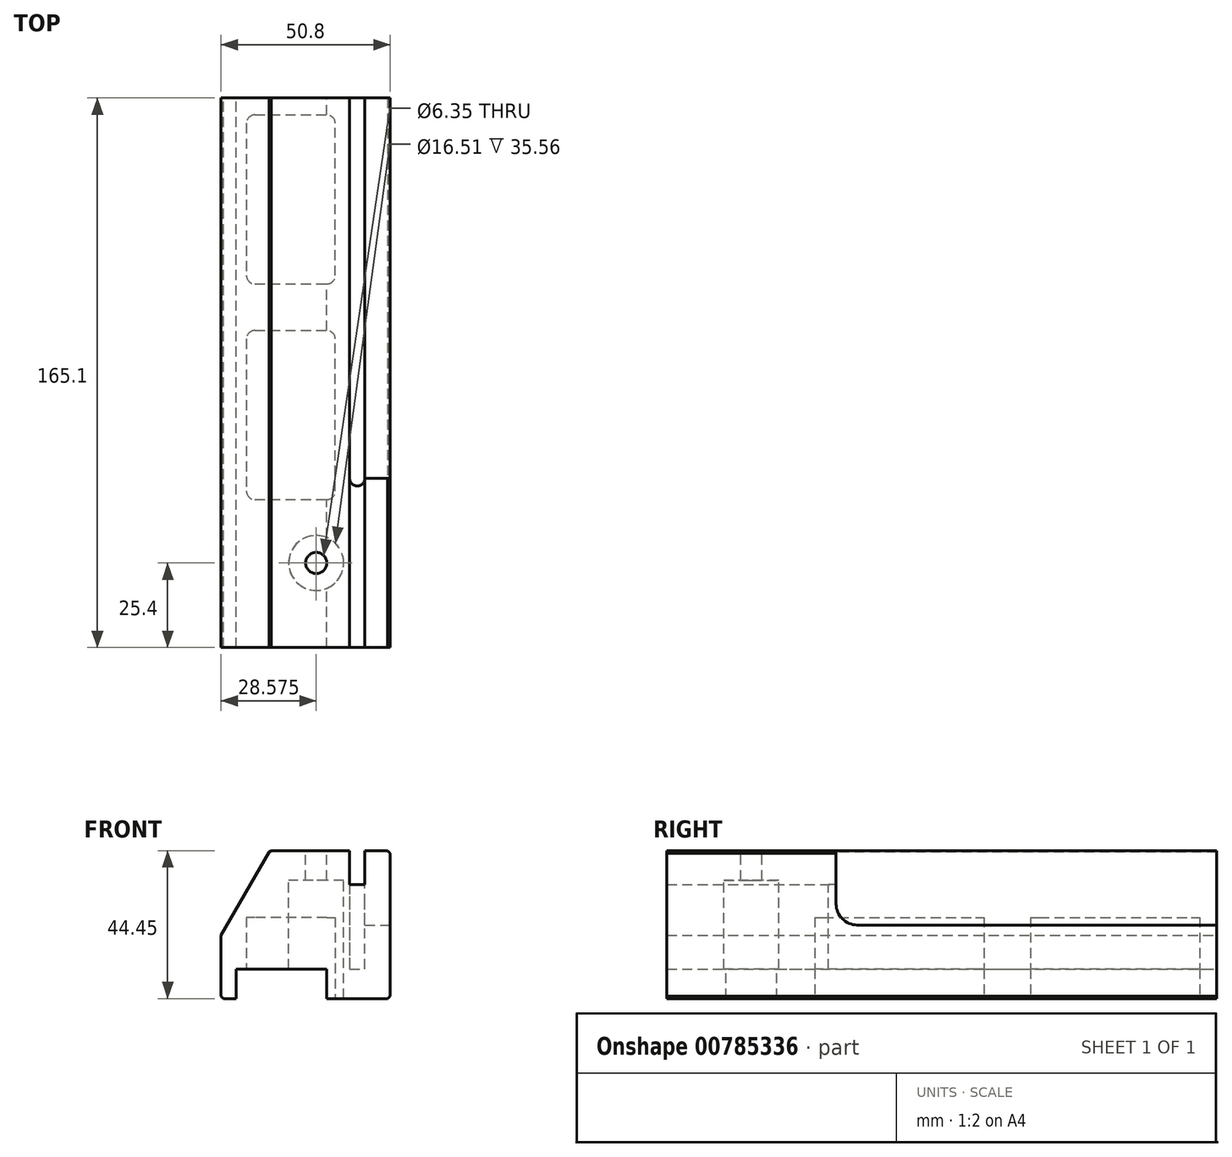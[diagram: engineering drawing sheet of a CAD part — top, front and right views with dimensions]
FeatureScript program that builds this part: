
annotation { "Feature Type Name" : "Feature", "Feature Type Description" : "" }
export const myFeature = defineFeature(function(context is Context, id is Id, definition is map)
    precondition{}
    {
        {
            var Q0;
            Q0=qCreatedBy(makeId("Front.planeOp"),FACE);
            var sketch = newSketch(context, id + "F0", { "sketchPlane" : qUnion([Q0])});
            skLineSegment(sketch, "E0.bottom", {"start": v(0, 0) * mm, "end": v(50.8, 0) * mm});
            skLineSegment(sketch, "E0.top", {"start": v(0, 44.45) * mm, "end": v(50.8, 44.45) * mm});
            skLineSegment(sketch, "E0.left", {"start": v(0, 0) * mm, "end": v(0, 44.45) * mm});
            skLineSegment(sketch, "E0.right", {"start": v(50.8, 0) * mm, "end": v(50.8, 44.45) * mm});
            skSolve(sketch);
        }
        {
            var Q0;
            Q0=qCreatedBy(makeId("Front.planeOp"),FACE);
            var sketch = newSketch(context, id + "F1", { "sketchPlane" : qUnion([Q0])});
            skLineSegment(sketch, "E1.bottom", {"start": v(4.57, 0) * mm, "end": v(31.75, 0) * mm});
            skLineSegment(sketch, "E1.top", {"start": v(4.57, 8.9) * mm, "end": v(31.75, 8.9) * mm});
            skLineSegment(sketch, "E1.left", {"start": v(4.57, 0) * mm, "end": v(4.57, 8.9) * mm});
            skLineSegment(sketch, "E1.right", {"start": v(31.75, 0) * mm, "end": v(31.75, 8.9) * mm});
            skSolve(sketch);
        }
        {
            var Q0;
            Q0=qCreatedBy(makeId("Front.planeOp"),FACE);
            var sketch = newSketch(context, id + "F2", { "sketchPlane" : qUnion([Q0])});
            skLineSegment(sketch, "E2.bottom", {"start": v(38.6, 44.45) * mm, "end": v(43.18, 44.45) * mm});
            skLineSegment(sketch, "E2.top", {"start": v(38.6, 34.3) * mm, "end": v(43.18, 34.3) * mm});
            skLineSegment(sketch, "E2.left", {"start": v(38.6, 44.45) * mm, "end": v(38.6, 34.3) * mm});
            skLineSegment(sketch, "E2.right", {"start": v(43.18, 44.45) * mm, "end": v(43.18, 34.3) * mm});
            skSolve(sketch);
        }
        {
            var Q0;
            Q0=qSketchRegion(id+"F0",true);
            extrude(context, id + "F3", {"entities" : qUnion([Q0]), "depth" : 165.1 * mm, "offsetDistance" : 25.4 * mm});
        }
        {
            var Q0;
            Q0=makeQuery(id+"F3.opExtrude","SWEPT_EDGE",EDGE,{"disambiguationData":[OSD([sQuery(id+"F0.wireOp",EDGE,"E0.top"),sQuery(id+"F0.wireOp",EDGE,"E0.left")])]});
            chamfer(context, id + "F4", {"entities" : qUnion([Q0]), "chamferType" : ChamferType.OFFSET_ANGLE, "width" : 25.4 * mm, "oppositeDirection" : false, "angle" : 30 * degree, "tangentPropagation" : true});
        }
        {
            var Q0;
            Q0=qSketchRegion(id+"F1",true);
            extrude(context, id + "F5", {"entities" : qUnion([Q0]), "operationType" : NewBodyOperationType.REMOVE, "depth" : 228.6 * mm, "offsetDistance" : 25.4 * mm});
        }
        {
            var Q0;
            Q0=qSketchRegion(id+"F2",true);
            extrude(context, id + "F6", {"entities" : qUnion([Q0]), "operationType" : NewBodyOperationType.REMOVE, "depth" : 228.6 * mm, "offsetDistance" : 25.4 * mm});
        }
        {
            var Q0;
            {var subQ0=sQuery(id+"F0.wireOp",EDGE,"E0.right");var subQ3=sQuery(id+"F0.wireOp",EDGE,"E0.bottom");Q0=makeQuery(id+"F5.boolean.opBoolean","SPLIT",FACE,{"disambiguationData":[TD([makeQuery(id+"F3.opExtrude","SWEPT_FACE",FACE,{"disambiguationData":[OSD([subQ0])]})])],"derivedFrom":makeQuery(id+"F3.opExtrude","SWEPT_FACE",FACE,{"disambiguationData":[OSD([subQ3])]})});}
            var sketch = newSketch(context, id + "F7", { "sketchPlane" : qUnion([Q0])});
            skLineSegment(sketch, "E3.bottom", {"start": v(31.75, 55.88) * mm, "end": v(10.16, 55.88) * mm});
            skLineSegment(sketch, "E3.top", {"start": v(31.75, 5.08) * mm, "end": v(10.16, 5.08) * mm});
            skLineSegment(sketch, "E3.left", {"start": v(34.29, 53.34) * mm, "end": v(34.3, 7.62) * mm});
            skLineSegment(sketch, "E3.right", {"start": v(7.62, 53.34) * mm, "end": v(7.62, 7.62) * mm});
            skPoint(sketch, "E4.visualSharp", {"position": v(7.62, 55.88) * mm});
            skArc(sketch, "E4.filletArc", {"start": v(10.16, 55.88) * mm, "mid": v(8.36, 55.14) * mm, "end": v(7.62, 53.34) * mm});
            skPoint(sketch, "E5.visualSharp", {"position": v(34.29, 55.88) * mm});
            skArc(sketch, "E5.filletArc", {"start": v(34.3, 53.34) * mm, "mid": v(33.55, 55.14) * mm, "end": v(31.75, 55.88) * mm});
            skPoint(sketch, "E6.visualSharp", {"position": v(34.3, 5.08) * mm});
            skArc(sketch, "E6.filletArc", {"start": v(31.75, 5.08) * mm, "mid": v(33.55, 5.82) * mm, "end": v(34.3, 7.62) * mm});
            skPoint(sketch, "E7.visualSharp", {"position": v(7.62, 5.08) * mm});
            skArc(sketch, "E7.filletArc", {"start": v(7.62, 7.62) * mm, "mid": v(8.36, 5.82) * mm, "end": v(10.16, 5.08) * mm});
            skLineSegment(sketch, "E8.bottom", {"start": v(31.75, 120.65) * mm, "end": v(10.16, 120.65) * mm});
            skLineSegment(sketch, "E8.top", {"start": v(31.75, 69.85) * mm, "end": v(10.16, 69.85) * mm});
            skLineSegment(sketch, "E8.left", {"start": v(34.29, 118.11) * mm, "end": v(34.29, 72.4) * mm});
            skLineSegment(sketch, "E8.right", {"start": v(7.62, 118.11) * mm, "end": v(7.62, 72.4) * mm});
            skPoint(sketch, "E9.visualSharp", {"position": v(7.62, 120.65) * mm});
            skArc(sketch, "E9.filletArc", {"start": v(10.16, 120.65) * mm, "mid": v(8.36, 119.9) * mm, "end": v(7.62, 118.11) * mm});
            skPoint(sketch, "E10.visualSharp", {"position": v(34.29, 120.65) * mm});
            skArc(sketch, "E10.filletArc", {"start": v(34.29, 118.11) * mm, "mid": v(33.55, 119.9) * mm, "end": v(31.75, 120.65) * mm});
            skPoint(sketch, "E11.visualSharp", {"position": v(34.29, 69.85) * mm});
            skArc(sketch, "E11.filletArc", {"start": v(31.75, 69.85) * mm, "mid": v(33.55, 70.6) * mm, "end": v(34.29, 72.4) * mm});
            skPoint(sketch, "E12.visualSharp", {"position": v(7.62, 69.85) * mm});
            skArc(sketch, "E12.filletArc", {"start": v(7.62, 72.4) * mm, "mid": v(8.36, 70.6) * mm, "end": v(10.16, 69.85) * mm});
            skSolve(sketch);
        }
        {
            var Q0;
            Q0=qSketchRegion(id+"F7",true);
            extrude(context, id + "F8", {"entities" : qUnion([Q0]), "operationType" : NewBodyOperationType.REMOVE, "oppositeDirection" : true, "depth" : 24.38 * mm, "offsetDistance" : 25.4 * mm});
        }
        {
            var Q0;
            Q0=makeQuery(id+"F3.opExtrude","SWEPT_FACE",FACE,{"disambiguationData":[OSD([sQuery(id+"F0.wireOp",EDGE,"E0.right")])]});
            var sketch = newSketch(context, id + "F9", { "sketchPlane" : qUnion([Q0])});
            skLineSegment(sketch, "E13.bottom", {"start": v(0, 44.45) * mm, "end": v(-114.3, 44.45) * mm});
            skLineSegment(sketch, "E13.top", {"start": v(0, 22.1) * mm, "end": v(-107.95, 22.1) * mm});
            skLineSegment(sketch, "E13.left", {"start": v(0, 44.45) * mm, "end": v(0, 22.1) * mm});
            skLineSegment(sketch, "E13.right", {"start": v(-114.3, 44.45) * mm, "end": v(-114.3, 28.45) * mm});
            skLineSegment(sketch, "E14.bottom", {"start": v(9.26, 33.5) * mm, "end": v(11.62, 33.5) * mm});
            skLineSegment(sketch, "E14.top", {"start": v(9.26, 34.28) * mm, "end": v(11.62, 34.28) * mm});
            skLineSegment(sketch, "E14.left", {"start": v(9.26, 33.5) * mm, "end": v(9.26, 34.28) * mm});
            skLineSegment(sketch, "E14.right", {"start": v(11.62, 33.5) * mm, "end": v(11.62, 34.28) * mm});
            skPoint(sketch, "E15.visualSharp", {"position": v(-114.3, 22.1) * mm});
            skArc(sketch, "E15.filletArc", {"start": v(-114.3, 28.45) * mm, "mid": v(-112.44, 23.96) * mm, "end": v(-107.95, 22.1) * mm});
            skSolve(sketch);
        }
        {
            var Q0;
            Q0=qSketchRegion(id+"F9",true);
            extrude(context, id + "F10", {"entities" : qUnion([Q0]), "operationType" : NewBodyOperationType.REMOVE, "oppositeDirection" : true, "depth" : 12.2 * mm, "offsetDistance" : 25.4 * mm});
        }
        {
            var Q0;
            {var subQ2=sQuery(id+"F0.wireOp",EDGE,"E0.top");Q0=makeQuery(id+"F6.boolean.opBoolean","SPLIT",FACE,{"disambiguationData":[TD([makeQuery(id+"F6.opExtrude","SWEPT_FACE",FACE,{"disambiguationData":[OSD([sQuery(id+"F2.wireOp",EDGE,"E2.left")])]})])],"derivedFrom":makeQuery(id+"F3.opExtrude","SWEPT_FACE",FACE,{"disambiguationData":[OSD([subQ2])]})});}
            var sketch = newSketch(context, id + "F11", { "sketchPlane" : qUnion([Q0])});
            skLineSegment(sketch, "E16.bottom", {"start": v(38.6, 0) * mm, "end": v(43.18, 0) * mm});
            skLineSegment(sketch, "E16.top", {"start": v(40.9, -116.59) * mm, "end": v(40.9, -116.59) * mm});
            skLineSegment(sketch, "E16.left", {"start": v(38.6, 0) * mm, "end": v(38.6, -114.3) * mm});
            skLineSegment(sketch, "E16.right", {"start": v(43.18, 0) * mm, "end": v(43.18, -114.3) * mm});
            skPoint(sketch, "E17.visualSharp", {"position": v(38.6, -116.59) * mm});
            skArc(sketch, "E17.filletArc", {"start": v(38.6, -114.3) * mm, "mid": v(39.28, -115.92) * mm, "end": v(40.9, -116.59) * mm});
            skPoint(sketch, "E18.visualSharp", {"position": v(43.18, -116.59) * mm});
            skArc(sketch, "E18.filletArc", {"start": v(40.9, -116.59) * mm, "mid": v(42.51, -115.92) * mm, "end": v(43.18, -114.3) * mm});
            skSolve(sketch);
        }
        {
            var Q0;
            Q0=qSketchRegion(id+"F11",true);
            extrude(context, id + "F12", {"entities" : qUnion([Q0]), "operationType" : NewBodyOperationType.REMOVE, "oppositeDirection" : true, "depth" : 35.56 * mm, "offsetDistance" : 25.4 * mm});
        }
        {
            var Q0;
            {var subQ0=sQuery(id+"F0.wireOp",EDGE,"E0.right");var subQ3=sQuery(id+"F0.wireOp",EDGE,"E0.bottom");Q0=makeQuery(id+"F5.boolean.opBoolean","SPLIT",FACE,{"disambiguationData":[TD([makeQuery(id+"F3.opExtrude","SWEPT_FACE",FACE,{"disambiguationData":[OSD([subQ0])]})])],"derivedFrom":makeQuery(id+"F3.opExtrude","SWEPT_FACE",FACE,{"disambiguationData":[OSD([subQ3])]})});}
            var sketch = newSketch(context, id + "F13", { "sketchPlane" : qUnion([Q0])});
            skCircle(sketch, "E19", {"center": v(28.58, 139.7) * mm, "radius": 4.2 * mm});
            skSolve(sketch);
        }
        {
            var Q0;
            Q0=sQuery(id+"F13.wireOp",VERTEX,"E19.center");
            var Q1;
            Q1=makeQuery(id+"F3.opExtrude","SWEPT_BODY",BODY,{"disambiguationData":[OSD([sQuery(id+"F0.wireOp",EDGE,"E0.bottom"),sQuery(id+"F0.wireOp",EDGE,"E0.top"),sQuery(id+"F0.wireOp",EDGE,"E0.left"),sQuery(id+"F0.wireOp",EDGE,"E0.right")])]});
            hole(context, id + "F14", {"style" : HoleStyle.C_BORE, "endStyle" : HoleEndStyle.THROUGH, "holeDiameter" : 6.35 * mm, "cBoreDiameter" : 16.5 * mm, "cBoreDepth" : 35.56 * mm, "majorDiameter" : 6.35 * mm, "isTappedThrough" : true, "tappedDepth" : 12.7 * mm, "tapClearance" : 3, "startFromSketch" : true, "locations" : qUnion([Q0]), "scope" : qUnion([Q1])});
        }
        {
            var Q0;
            {var subQ0=sQuery(id+"F0.wireOp",EDGE,"E0.top");Q0=makeQuery(id+"F4.opChamfer","BLEND_EDGE",EDGE,{"blendedFrom":[makeQuery(id+"F3.opExtrude","SWEPT_EDGE",EDGE,{"disambiguationData":[OSD([subQ0,sQuery(id+"F0.wireOp",EDGE,"E0.left")])]}),makeQuery(id+"F3.opExtrude","SWEPT_FACE",FACE,{"disambiguationData":[OSD([subQ0])]})],"blendedInto":[makeQuery(id+"F3.opExtrude","SWEPT_FACE",FACE,{"disambiguationData":[OSD([subQ0])]})]});}
            var Q1;
            Q1=makeQuery(id+"F3.opExtrude","SWEPT_EDGE",EDGE,{"disambiguationData":[OSD([sQuery(id+"F0.wireOp",EDGE,"E0.top"),sQuery(id+"F0.wireOp",EDGE,"E0.right")])]});
            var Q2;
            Q2=makeQuery(id+"F6.boolean.opBoolean","COPY",EDGE,{"derivedFrom":makeQuery(id+"F6.opExtrude","SWEPT_EDGE",EDGE,{"disambiguationData":[OSD([sQuery(id+"F2.wireOp",EDGE,"E2.bottom"),sQuery(id+"F2.wireOp",EDGE,"E2.left")])]})});
            var Q3;
            Q3=makeQuery(id+"F6.boolean.opBoolean","COPY",EDGE,{"derivedFrom":makeQuery(id+"F6.opExtrude","SWEPT_EDGE",EDGE,{"disambiguationData":[OSD([sQuery(id+"F2.wireOp",EDGE,"E2.bottom"),sQuery(id+"F2.wireOp",EDGE,"E2.right")])]})});
            var Q4;
            Q4=makeQuery(id+"F3.opExtrude","SWEPT_EDGE",EDGE,{"disambiguationData":[OSD([sQuery(id+"F0.wireOp",EDGE,"E0.bottom"),sQuery(id+"F0.wireOp",EDGE,"E0.right")])]});
            var Q5;
            Q5=makeQuery(id+"F3.opExtrude","SWEPT_EDGE",EDGE,{"disambiguationData":[OSD([sQuery(id+"F0.wireOp",EDGE,"E0.bottom"),sQuery(id+"F0.wireOp",EDGE,"E0.left")])]});
            chamfer(context, id + "F15", {"entities" : qUnion([Q0, Q1, Q2, Q3, Q4, Q5]), "width" : 0.76 * mm, "tangentPropagation" : true});
        }
    });
